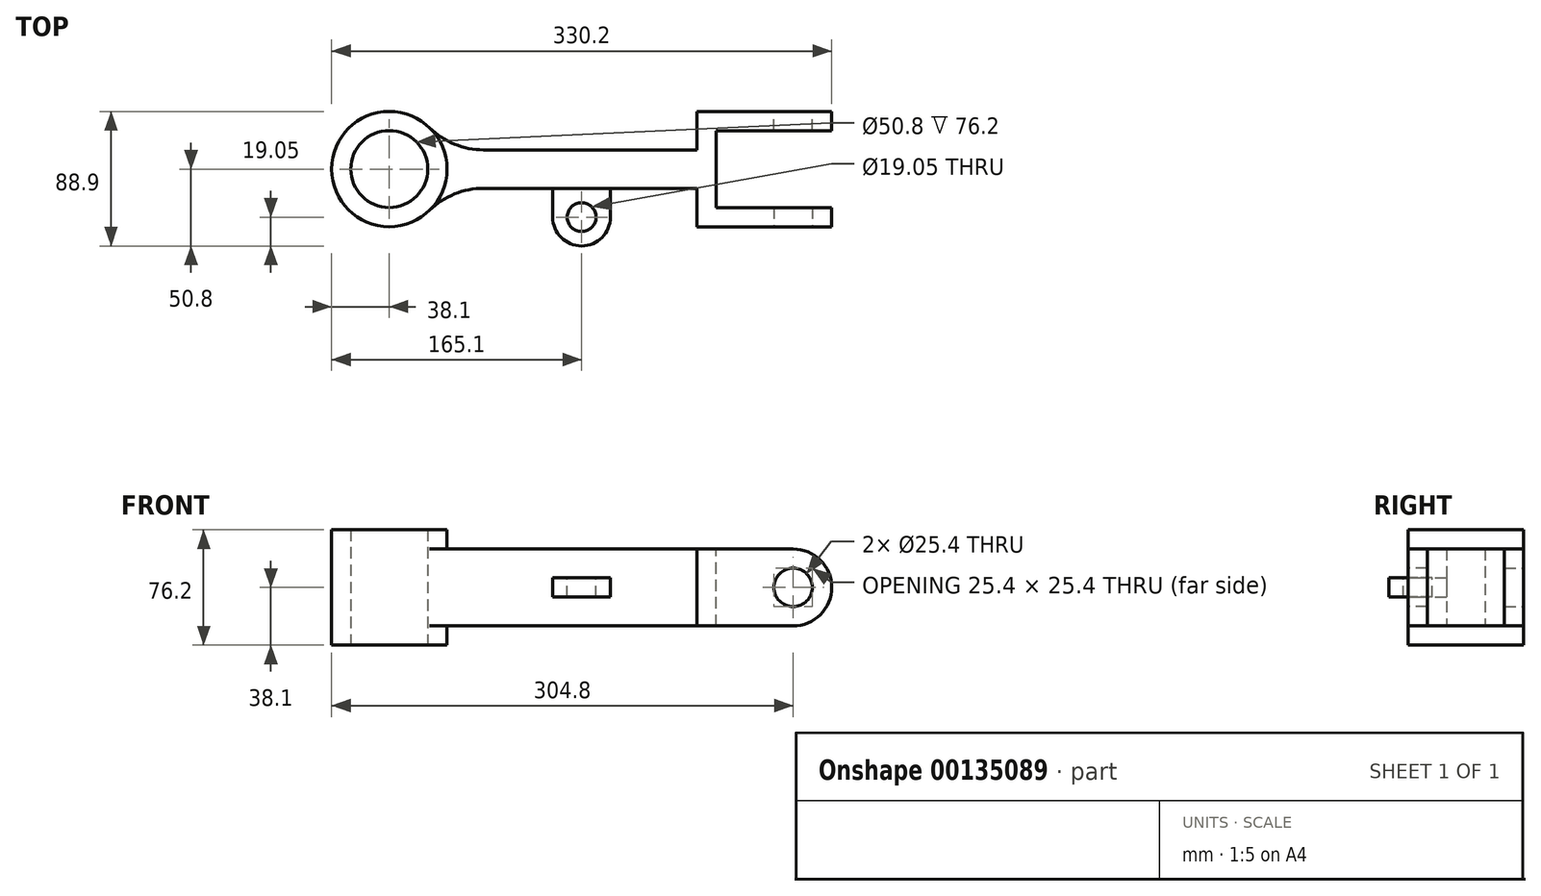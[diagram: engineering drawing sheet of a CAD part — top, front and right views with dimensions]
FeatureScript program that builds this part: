
annotation { "Feature Type Name" : "Feature", "Feature Type Description" : "" }
export const myFeature = defineFeature(function(context is Context, id is Id, definition is map)
    precondition{}
    {
        {
            var Q0;
            Q0=qCreatedBy(makeId("Top.planeOp"),FACE);
            var sketch = newSketch(context, id + "F0", { "sketchPlane" : qUnion([Q0])});
            skArc(sketch, "E0", {"start": v(-38.1, 0) * mm, "mid": v(0, -38.1) * mm, "end": v(38.1, 0) * mm});
            skLineSegment(sketch, "E1", {"start": v(-38.1, 0) * mm, "end": v(-25.4, 0) * mm});
            skLineSegment(sketch, "E2", {"start": v(203.2, 0) * mm, "end": v(203.2, -12.7) * mm});
            skLineSegment(sketch, "E3", {"start": v(203.2, -12.7) * mm, "end": v(35.92, -12.7) * mm});
            skArc(sketch, "E4", {"start": v(-25.4, 0) * mm, "mid": v(0, -25.4) * mm, "end": v(25.4, 0) * mm});
            skLineSegment(sketch, "E5.trimOffspring", {"start": v(25.4, 0) * mm, "end": v(203.2, 0) * mm});
            skSolve(sketch);
        }
        {
            var Q0;
            Q0 = qSketchRegion(id + "F0", true);
            extrude(context, id + "F1", {"entities" : qUnion([Q0]), "depth" : 76.2 * mm});
        }
        {
            var Q0;
            Q0=makeQuery(id+"F1.opExtrude","CAP_FACE",FACE,{"disambiguationData":[OSD([sQuery(id+"F0.wireOp",EDGE,"E0"),sQuery(id+"F0.wireOp",EDGE,"E1"),sQuery(id+"F0.wireOp",EDGE,"E2"),sQuery(id+"F0.wireOp",EDGE,"E3"),sQuery(id+"F0.wireOp",EDGE,"E4"),sQuery(id+"F0.wireOp",EDGE,"E5.trimOffspring")])],"isStart":false});
            var sketch = newSketch(context, id + "F2", { "sketchPlane" : qUnion([Q0])});
            skArc(sketch, "E6.0", {"start": v(35.92, -12.7) * mm, "mid": v(37.55, -6.44) * mm, "end": v(38.1, 0) * mm});
            skLineSegment(sketch, "E7.0", {"start": v(203.2, -12.7) * mm, "end": v(35.92, -12.7) * mm});
            skLineSegment(sketch, "E8.0", {"start": v(38.1, 0) * mm, "end": v(203.2, 0) * mm});
            skLineSegment(sketch, "E9.0", {"start": v(203.2, 0) * mm, "end": v(203.2, -12.7) * mm});
            skPoint(sketch, "E10.orphan", {"position": v(-38.1, 0) * mm});
            skSolve(sketch);
        }
        {
            var Q0;
            Q0 = qSketchRegion(id + "F2", true);
            extrude(context, id + "F3", {"entities" : qUnion([Q0]), "operationType" : NewBodyOperationType.REMOVE, "oppositeDirection" : true, "depth" : 12.7 * mm});
        }
        {
            var Q0;
            {var subQ4=sQuery(id+"F0.wireOp",EDGE,"E2");Q0=makeQuery(id+"F0.imprint","IMPRINT",FACE,{"disambiguationData":[TD([[makeQuery(id+"F0.imprint","IMPRINT",EDGE,{"derivedFrom":subQ4}),-1.0]])]});}
            extrude(context, id + "F4", {"entities" : qUnion([Q0]), "operationType" : NewBodyOperationType.REMOVE, "depth" : 12.7 * mm});
        }
        {
            var Q0;
            Q0=makeQuery(id+"F1.opExtrude","SWEPT_EDGE",EDGE,{"disambiguationData":[OSD([sQuery(id+"F0.wireOp",EDGE,"E0"),sQuery(id+"F0.wireOp",EDGE,"E3")])]});
            fillet(context, id + "F5", {"entities" : qUnion([Q0]), "radius" : 50.8 * mm, "tangentPropagation" : true, "allowEdgeOverflow" : false});
        }
        {
            var Q0;
            Q0=makeQuery(id+"F3.boolean.opBoolean","COPY",FACE,{"derivedFrom":makeQuery(id+"F3.opExtrude","CAP_FACE",FACE,{"disambiguationData":[OSD([sQuery(id+"F2.wireOp",EDGE,"E6.0"),sQuery(id+"F2.wireOp",EDGE,"E7.0"),sQuery(id+"F2.wireOp",EDGE,"E8.0"),sQuery(id+"F2.wireOp",EDGE,"E9.0")])],"isStart":false})});
            var sketch = newSketch(context, id + "F6", { "sketchPlane" : qUnion([Q0])});
            skLineSegment(sketch, "E11.0", {"start": v(203.2, 0) * mm, "end": v(203.2, -12.7) * mm});
            skLineSegment(sketch, "E12", {"start": v(203.2, -12.7) * mm, "end": v(203.2, -38.1) * mm});
            skLineSegment(sketch, "E13", {"start": v(203.2, -38.1) * mm, "end": v(292.1, -38.1) * mm});
            skLineSegment(sketch, "E14", {"start": v(292.1, -38.1) * mm, "end": v(292.1, -25.4) * mm});
            skLineSegment(sketch, "E15", {"start": v(292.1, -25.4) * mm, "end": v(215.9, -25.4) * mm});
            skLineSegment(sketch, "E16", {"start": v(215.9, -25.4) * mm, "end": v(215.9, 0) * mm});
            skLineSegment(sketch, "E17", {"start": v(215.9, 0) * mm, "end": v(203.2, 0) * mm});
            skSolve(sketch);
        }
        {
            var Q0;
            Q0 = qSketchRegion(id + "F6", true);
            var Q1;
            Q1=makeQuery(id+"F4.boolean.opBoolean","COPY",FACE,{"derivedFrom":makeQuery(id+"F4.opExtrude","CAP_FACE",FACE,{"disambiguationData":[OSD([sQuery(id+"F0.wireOp",EDGE,"E0"),sQuery(id+"F0.wireOp",EDGE,"E2"),sQuery(id+"F0.wireOp",EDGE,"E3"),sQuery(id+"F0.wireOp",EDGE,"E5.trimOffspring")])],"isStart":false})});
            extrude(context, id + "F7", {"entities" : qUnion([Q0]), "operationType" : NewBodyOperationType.ADD, "endBound" : BoundingType.UP_TO_SURFACE, "oppositeDirection" : true, "endBoundEntityFace" : qUnion([Q1]), "depth" : 25.4 * mm});
        }
        {
            var Q0;
            Q0=makeQuery(id+"F7.opExtrude","CAP_EDGE",EDGE,{"disambiguationData":[OSD([sQuery(id+"F6.wireOp",EDGE,"E14")])],"isStart":true});
            var Q1;
            Q1=makeQuery(id+"F7.opExtrude","CAP_EDGE",EDGE,{"disambiguationData":[OSD([sQuery(id+"F6.wireOp",EDGE,"E14")])],"isStart":false});
            fillet(context, id + "F8", {"entities" : qUnion([Q0, Q1]), "radius" : 25.4 * mm, "tangentPropagation" : true, "allowEdgeOverflow" : false});
        }
        {
            var Q0;
            Q0=makeQuery(id+"F7.opExtrude","SWEPT_FACE",FACE,{"disambiguationData":[OSD([sQuery(id+"F6.wireOp",EDGE,"E13")])]});
            var sketch = newSketch(context, id + "F9", { "sketchPlane" : qUnion([Q0])});
            skArc(sketch, "E18.0", {"start": v(266.7, 12.7) * mm, "mid": v(292.1, 38.1) * mm, "end": v(266.7, 63.5) * mm});
            skCircle(sketch, "E19", {"center": v(266.7, 38.1) * mm, "radius": 12.7 * mm});
            skSolve(sketch);
        }
        {
            var Q0;
            Q0 = qSketchRegion(id + "F9", true);
            var Q1;
            Q1=makeQuery(id+"F7.opExtrude","SWEPT_FACE",FACE,{"disambiguationData":[OSD([sQuery(id+"F6.wireOp",EDGE,"E15")])]});
            extrude(context, id + "F10", {"entities" : qUnion([Q0]), "operationType" : NewBodyOperationType.REMOVE, "endBound" : BoundingType.UP_TO_SURFACE, "oppositeDirection" : true, "endBoundEntityFace" : qUnion([Q1]), "depth" : 25.4 * mm});
        }
        {
            var Q0;
            Q0=makeQuery(id+"F1.opExtrude","SWEPT_BODY",BODY,{"disambiguationData":[OSD([sQuery(id+"F0.wireOp",EDGE,"E0"),sQuery(id+"F0.wireOp",EDGE,"E1"),sQuery(id+"F0.wireOp",EDGE,"E2"),sQuery(id+"F0.wireOp",EDGE,"E3"),sQuery(id+"F0.wireOp",EDGE,"E4"),sQuery(id+"F0.wireOp",EDGE,"E5.trimOffspring")])]});
            var Q1;
            Q1=qCreatedBy(makeId("Front.planeOp"),FACE);
            mirror(context, id + "F11", {"operationType" : NewBodyOperationType.ADD, "entities" : qUnion([Q0]), "mirrorPlane" : qUnion([Q1])});
        }
        {
            var Q0;
            Q0=makeQuery(id+"F1.opExtrude","SWEPT_FACE",FACE,{"disambiguationData":[OSD([sQuery(id+"F0.wireOp",EDGE,"E3")])]});
            var sketch = newSketch(context, id + "F12", { "sketchPlane" : qUnion([Q0])});
            skLineSegment(sketch, "E20.0", {"start": v(62.22, 63.5) * mm, "end": v(62.22, 12.7) * mm, "construction": true});
            skLineSegment(sketch, "E21.0", {"start": v(203.2, 63.5) * mm, "end": v(62.22, 63.5) * mm, "construction": true});
            skLineSegment(sketch, "E22.0", {"start": v(203.2, 12.7) * mm, "end": v(203.2, 63.5) * mm, "construction": true});
            skLineSegment(sketch, "E23.0", {"start": v(203.2, 12.7) * mm, "end": v(62.22, 12.7) * mm, "construction": true});
            skPoint(sketch, "E24", {"position": v(127, 44.45) * mm});
            skLineSegment(sketch, "E25", {"start": v(127, 44.45) * mm, "end": v(146.05, 44.45) * mm});
            skLineSegment(sketch, "E26", {"start": v(146.05, 44.45) * mm, "end": v(146.05, 31.75) * mm});
            skLineSegment(sketch, "E27", {"start": v(146.05, 31.75) * mm, "end": v(127, 31.75) * mm});
            skLineSegment(sketch, "E28", {"start": v(127, 44.45) * mm, "end": v(127, 31.75) * mm, "construction": true});
            skLineSegment(sketch, "E29.MirrorCS", {"start": v(127, 44.45) * mm, "end": v(107.95, 44.45) * mm});
            skLineSegment(sketch, "E30.MirrorCS", {"start": v(107.95, 44.45) * mm, "end": v(107.95, 31.75) * mm});
            skLineSegment(sketch, "E31.MirrorCS", {"start": v(107.95, 31.75) * mm, "end": v(127, 31.75) * mm});
            skSolve(sketch);
        }
        {
            var Q0;
            Q0 = qSketchRegion(id + "F12", true);
            extrude(context, id + "F13", {"entities" : qUnion([Q0]), "operationType" : NewBodyOperationType.ADD, "depth" : 38.1 * mm});
        }
        {
            var Q0;
            Q0=makeQuery(id+"F13.opExtrude","CAP_EDGE",EDGE,{"disambiguationData":[OSD([sQuery(id+"F12.wireOp",EDGE,"E30.MirrorCS")])],"isStart":false});
            var Q1;
            Q1=makeQuery(id+"F13.opExtrude","CAP_EDGE",EDGE,{"disambiguationData":[OSD([sQuery(id+"F12.wireOp",EDGE,"E26")])],"isStart":false});
            fillet(context, id + "F14", {"entities" : qUnion([Q0, Q1]), "radius" : 19.05 * mm, "tangentPropagation" : true, "allowEdgeOverflow" : false});
        }
        {
            var Q0;
            Q0=makeQuery(id+"F13.opExtrude","SWEPT_FACE",FACE,{"disambiguationData":[OSD([sQuery(id+"F12.wireOp",EDGE,"E25"),sQuery(id+"F12.wireOp",EDGE,"E29.MirrorCS")])]});
            var sketch = newSketch(context, id + "F15", { "sketchPlane" : qUnion([Q0])});
            skArc(sketch, "E32.0", {"start": v(107.95, -31.75) * mm, "mid": v(127, -50.8) * mm, "end": v(146.05, -31.75) * mm});
            skCircle(sketch, "E33", {"center": v(127, -31.75) * mm, "radius": 9.53 * mm});
            skSolve(sketch);
        }
        {
            var Q0;
            Q0 = qSketchRegion(id + "F15", true);
            var Q1;
            Q1=makeQuery(id+"F13.opExtrude","SWEPT_FACE",FACE,{"disambiguationData":[OSD([sQuery(id+"F12.wireOp",EDGE,"E27"),sQuery(id+"F12.wireOp",EDGE,"E31.MirrorCS")])]});
            extrude(context, id + "F16", {"entities" : qUnion([Q0]), "operationType" : NewBodyOperationType.REMOVE, "endBound" : BoundingType.UP_TO_SURFACE, "oppositeDirection" : true, "endBoundEntityFace" : qUnion([Q1]), "depth" : 25.4 * mm});
        }
    });
